# Revit family: BuroSeating_Konfurb Star_A
name_source: partatom
category: Furniture
units: mm (PartAtom-declared; Revit-internal decimal feet)

## family parameters
Always vertical = Yes
Cut with Voids When Loaded = No
OmniClass Number = 23.40.70.14.64.11
OmniClass Title = Office Furniture
Room Calculation Point = No
Shared = No
Work Plane-Based = No

## types (3) — shared parameters
Assembly Code = E2020
BackRestStar_1 = Yes
BaseOffset = 18 mm  [stored 0.0590551 ft]
FeetDiameter = 35 mm  [stored 0.114829 ft]
Manufacturer = Buro Seating
NominalHeight = 750 mm  [stored 2.46063 ft]
NominalLength = 816 mm
NominalWidth = 858 mm  [stored 2.81496 ft]
ProductGroup = Star
ProductPageURL AU = https://buroseating.com
ProductPageURL NZ = https://buroseating.co.nz
ProductRange = Konfurb
SeatHeight = 450 mm  [stored 1.47638 ft]
URL = https://buroseating.co.nz
URL AU = https://buroseating.com
WarrantyDescription = Full 5 year guarantee (excluding upholstery)
zero-valued in all types: Default Elevation

## per-type parameters (varying)
| type | BackRestStar_2 | BackRestStar_3 | Description | FeetMaterial |
| KON723-A | No | No | Konfub Star A | BuroSeating_Plastic_Black |
| KON723-A MB | Yes | No | Konfub Star A Mid Back | <By Category> |
| KON723-A HB | Yes | Yes | Konfub Star A High Back | <By Category> |

note: column(s) folded — value = type name in every type: Model

note: [stored X ft] marks values corroborated as IEEE doubles in the binary element streams (Revit-internal decimal feet)

## geometry (parser evidence)
native form markers: Sweep x5
no freeform markers — native parametric forms only
